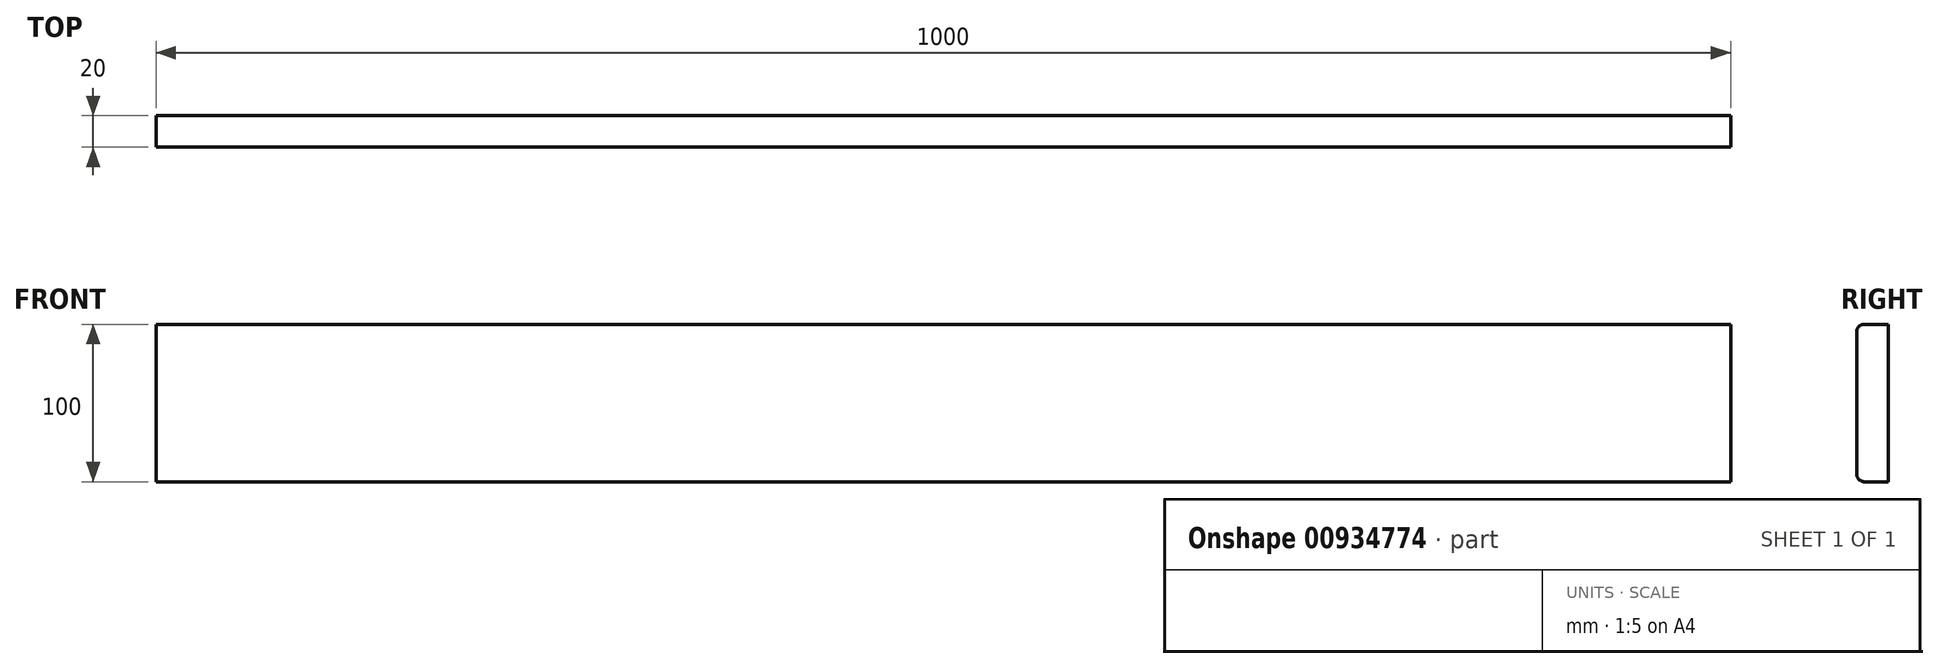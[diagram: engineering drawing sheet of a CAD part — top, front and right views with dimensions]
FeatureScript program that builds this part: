
annotation { "Feature Type Name" : "Feature", "Feature Type Description" : "" }
export const myFeature = defineFeature(function(context is Context, id is Id, definition is map)
    precondition{}
    {
        {
            var Q0;
            Q0=qCreatedBy(makeId("Front.planeOp"),FACE);
            var sketch = newSketch(context, id + "F0", { "sketchPlane" : qUnion([Q0])});
            skLineSegment(sketch, "E0.bottom", {"start": v(0, 0) * mm, "end": v(-1000, 0) * mm});
            skLineSegment(sketch, "E0.top", {"start": v(0, 100) * mm, "end": v(-1000, 100) * mm});
            skLineSegment(sketch, "E0.left", {"start": v(0, 0) * mm, "end": v(0, 100) * mm});
            skLineSegment(sketch, "E0.right", {"start": v(-1000, 0) * mm, "end": v(-1000, 100) * mm});
            skSolve(sketch);
        }
        {
            var Q0;
            Q0 = qSketchRegion(id + "F0", true);
            extrude(context, id + "F1", {"entities" : qUnion([Q0]), "depth" : 20 * mm, "offsetDistance" : 25 * mm});
        }
        {
            var Q0;
            Q0=makeQuery(id+"F1.opExtrude","CAP_EDGE",EDGE,{"disambiguationData":[OSD([sQuery(id+"F0.wireOp",EDGE,"E0.top")])],"isStart":false});
            var Q1;
            Q1=makeQuery(id+"F1.opExtrude","CAP_EDGE",EDGE,{"disambiguationData":[OSD([sQuery(id+"F0.wireOp",EDGE,"E0.bottom")])],"isStart":false});
            fillet(context, id + "F2", {"entities" : qUnion([Q0, Q1]), "radius" : 5 * mm, "tangentPropagation" : true, "allowEdgeOverflow" : false});
        }
    });
